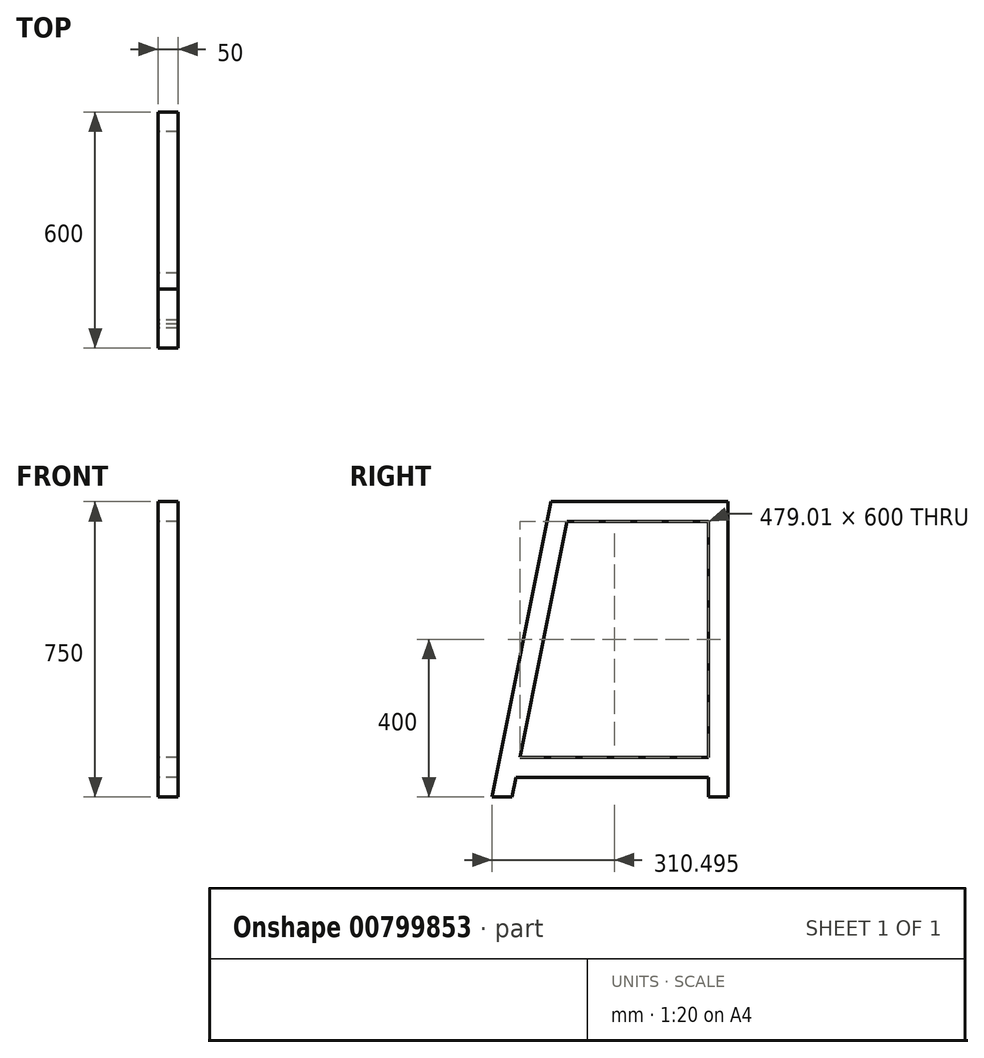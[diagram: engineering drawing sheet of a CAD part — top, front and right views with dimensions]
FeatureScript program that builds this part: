
annotation { "Feature Type Name" : "Feature", "Feature Type Description" : "" }
export const myFeature = defineFeature(function(context is Context, id is Id, definition is map)
    precondition{}
    {
        {
            var Q0;
            Q0=qCreatedBy(makeId("Right.planeOp"),FACE);
            var sketch = newSketch(context, id + "F0", { "sketchPlane" : qUnion([Q0])});
            skLineSegment(sketch, "E0", {"start": v(0, -750) * mm, "end": v(-50, -750) * mm});
            skLineSegment(sketch, "E1", {"start": v(-50, -750) * mm, "end": v(-50, -700) * mm});
            skLineSegment(sketch, "E2", {"start": v(-50, -700) * mm, "end": v(-539, -700) * mm});
            skLineSegment(sketch, "E3", {"start": v(-450, 0) * mm, "end": v(-600, -750) * mm});
            skLineSegment(sketch, "E4", {"start": v(-600, -750) * mm, "end": v(-549, -750) * mm});
            skLineSegment(sketch, "E5", {"start": v(-549, -750) * mm, "end": v(-539, -700) * mm});
            skLineSegment(sketch, "E6", {"start": v(-50, -650) * mm, "end": v(-50, -50) * mm});
            skLineSegment(sketch, "E7", {"start": v(-50, -50) * mm, "end": v(-409, -50) * mm});
            skLineSegment(sketch, "E8", {"start": v(-409, -50) * mm, "end": v(-529, -650) * mm});
            skLineSegment(sketch, "E9", {"start": v(-529, -650) * mm, "end": v(-50, -650) * mm});
            skLineSegment(sketch, "E10", {"start": v(0, -750) * mm, "end": v(0, 0) * mm});
            skLineSegment(sketch, "E11", {"start": v(0, 0) * mm, "end": v(-450, 0) * mm});
            skSolve(sketch);
        }
        {
            var Q0;
            Q0=makeQuery(id+"F0.imprint","IMPRINT",FACE,{"disambiguationData":[TD([[makeQuery(id+"F0.imprint","IMPRINT",EDGE,{"derivedFrom":sQuery(id+"F0.wireOp",EDGE,"E0")}),-1.0]])]});
            extrude(context, id + "F1", {"entities" : qUnion([Q0]), "depth" : 50 * mm, "offsetDistance" : 25 * mm});
        }
    });
